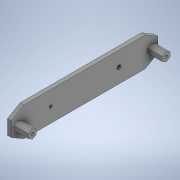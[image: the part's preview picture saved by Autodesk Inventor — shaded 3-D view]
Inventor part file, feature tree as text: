
AUTODESK INVENTOR PART (.ipt)
format: ipt  version: 2020 (Build 240168000, 168)  size: 251,904 bytes
history: native  units: in
note: dims shown in document units (in); Inventor stores cm internally (conversion verified against a paired STEP export)
features: extrude x7, sketch x7, plane x1
ambient origin geometry x8: Origin, YZ Plane, XZ Plane, XY Plane, X Axis, Y Axis, Z Axis, Center Point
bodies: Solid1 (feature_tree)
feature tree (15):
  extrude  "Extrusion1"  Depth=5.9055in
  extrude  "Extrusion3"  TaperAngle=0.0deg  [1 undecoded]
  extrude  "Extrusion4"  Depth=0.5906in
  plane  "Work Plane1"
  extrude  "Extrusion5"  Depth=0.122in
  extrude  "Extrusion6"  Depth=0.2402in
  extrude  "Extrusion7"  [1 undecoded]
  extrude  "Extrusion8"  Depth=0.0866in TaperAngle=0.0deg
  sketch  "Sketch1"  dims[d0=1.1811in d1=5.9055in]
  sketch  "Sketch2"  dims[d2=0.1575in d3=0.0in]
  sketch  "Sketch3"  dims[d8=0.315in d9=0.5906in]
  sketch  "Sketch4"  dims[d10=0.0in d12=0.122in]
  sketch  "Sketch5"  dims[d13=0.0in d14=0.0in d15=0.2402in]
  sketch  "Sketch8"  dims[d16=0.0866in d17=-0.2233in]
  sketch  "Sketch9"  dims[d18=-0.3937in d19=0.0866in d20=0.0in d26=1.5748in d27=0.1654in d28=0.122in d29=1.5748in d30=0.0in d31=0.0in d32=0.2402in d33=0.0866in d34=-0.2233in]
note: 2 required parameter values undecoded (feature->parameter linkage not recoverable at this tier; creation-order binding heuristic only, values carry confidence <= 0.55)
